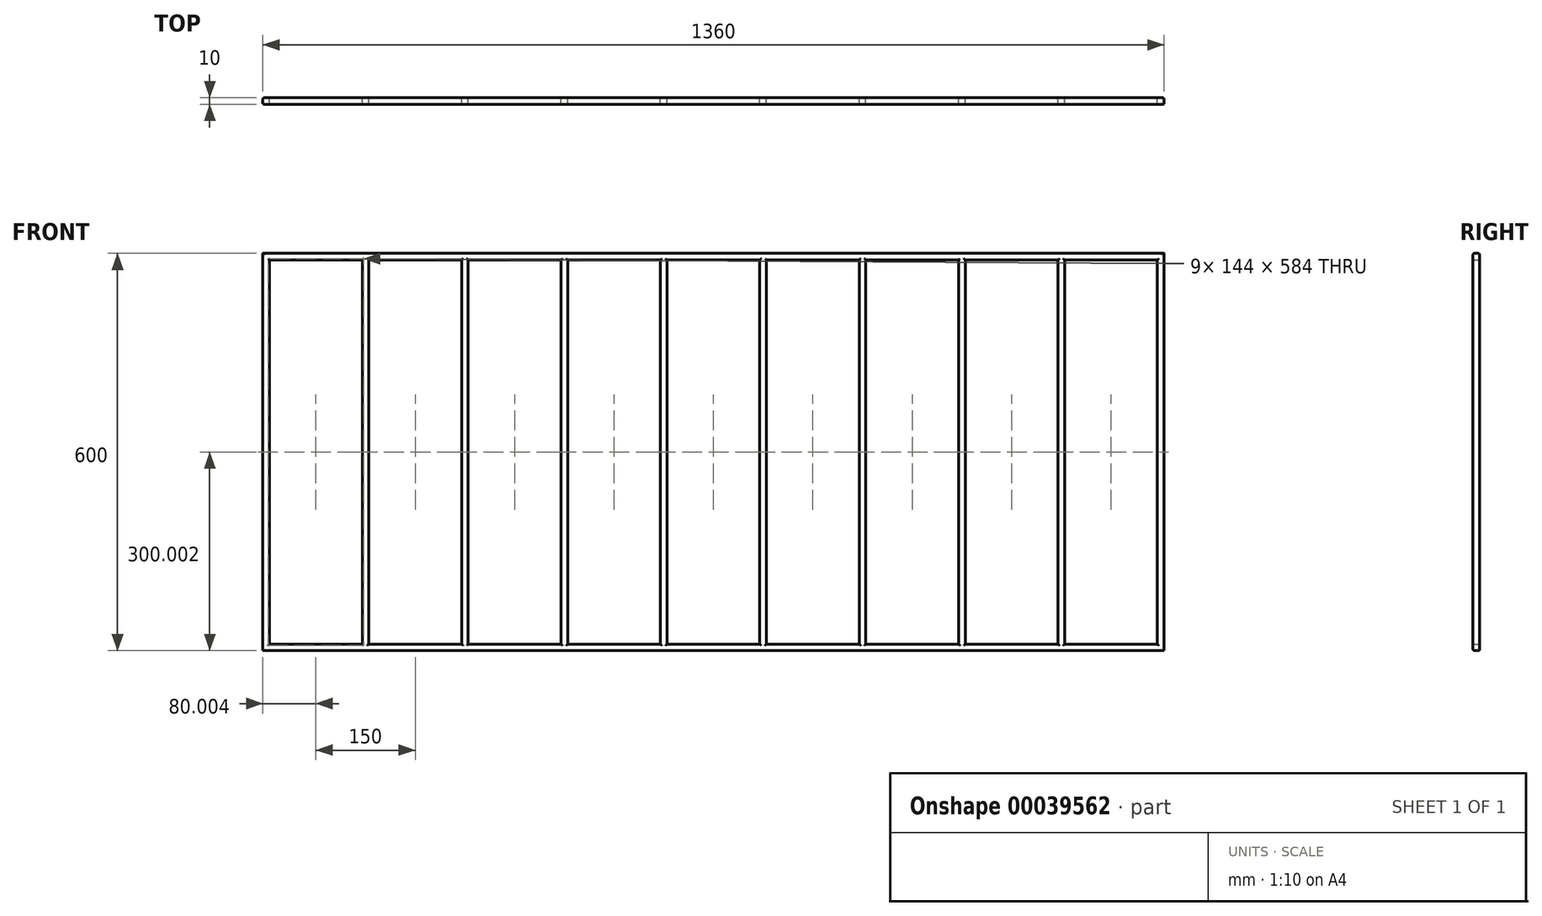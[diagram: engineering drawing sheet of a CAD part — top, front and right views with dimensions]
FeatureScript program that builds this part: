
annotation { "Feature Type Name" : "Feature", "Feature Type Description" : "" }
export const myFeature = defineFeature(function(context is Context, id is Id, definition is map)
    precondition{}
    {
        {
            var Q0;
            Q0=qCreatedBy(makeId("Front.planeOp"),FACE);
            var sketch = newSketch(context, id + "F0", { "sketchPlane" : qUnion([Q0])});
            skLineSegment(sketch, "E0.bottom", {"start": v(-58.93, -32.3) * mm, "end": v(1301.07, -32.3) * mm});
            skLineSegment(sketch, "E0.top", {"start": v(-58.93, 567.7) * mm, "end": v(1301.07, 567.7) * mm});
            skLineSegment(sketch, "E0.left", {"start": v(-58.93, -32.3) * mm, "end": v(-58.93, 567.7) * mm});
            skLineSegment(sketch, "E0.right", {"start": v(1301.07, -32.3) * mm, "end": v(1301.07, 567.7) * mm});
            skLineSegment(sketch, "E1.0", {"start": v(-48.93, 557.7) * mm, "end": v(91.07, 557.7) * mm});
            skLineSegment(sketch, "E2.0", {"start": v(-48.93, -22.3) * mm, "end": v(-48.93, 557.7) * mm});
            skLineSegment(sketch, "E3.0", {"start": v(1291.07, -22.3) * mm, "end": v(1291.07, 557.7) * mm});
            skLineSegment(sketch, "E4.0", {"start": v(-48.93, -22.3) * mm, "end": v(91.07, -22.3) * mm});
            skLineSegment(sketch, "E5.0", {"start": v(91.07, -22.3) * mm, "end": v(91.07, 557.7) * mm});
            skLineSegment(sketch, "E6.0", {"start": v(101.07, -22.3) * mm, "end": v(101.07, 557.7) * mm});
            skLineSegment(sketch, "E7.0", {"start": v(241.07, -22.3) * mm, "end": v(241.07, 557.7) * mm});
            skLineSegment(sketch, "E8.0", {"start": v(251.07, -22.3) * mm, "end": v(251.07, 557.7) * mm});
            skLineSegment(sketch, "E9.0", {"start": v(391.07, -22.3) * mm, "end": v(391.07, 557.7) * mm});
            skLineSegment(sketch, "E10.0", {"start": v(401.07, -22.3) * mm, "end": v(401.07, 557.7) * mm});
            skLineSegment(sketch, "E11.0", {"start": v(541.07, -22.3) * mm, "end": v(541.07, 557.7) * mm});
            skLineSegment(sketch, "E12.0", {"start": v(551.07, -22.3) * mm, "end": v(551.07, 557.7) * mm});
            skLineSegment(sketch, "E13.0", {"start": v(691.07, -22.3) * mm, "end": v(691.07, 557.7) * mm});
            skLineSegment(sketch, "E14.0", {"start": v(701.07, -22.3) * mm, "end": v(701.07, 557.7) * mm});
            skLineSegment(sketch, "E15.0", {"start": v(841.07, -22.3) * mm, "end": v(841.07, 557.7) * mm});
            skLineSegment(sketch, "E16.0", {"start": v(851.07, -22.3) * mm, "end": v(851.07, 557.7) * mm});
            skLineSegment(sketch, "E17.0", {"start": v(991.07, -22.3) * mm, "end": v(991.07, 557.7) * mm});
            skLineSegment(sketch, "E18.0", {"start": v(1001.07, -22.3) * mm, "end": v(1001.07, 557.7) * mm});
            skLineSegment(sketch, "E19.0", {"start": v(1141.07, -22.3) * mm, "end": v(1141.07, 557.7) * mm});
            skLineSegment(sketch, "E20.0", {"start": v(1151.07, -22.3) * mm, "end": v(1151.07, 557.7) * mm});
            skLineSegment(sketch, "E21.trimOffspring", {"start": v(101.07, 557.7) * mm, "end": v(241.07, 557.7) * mm});
            skLineSegment(sketch, "E22.trimOffspring", {"start": v(251.07, 557.7) * mm, "end": v(391.07, 557.7) * mm});
            skLineSegment(sketch, "E23.trimOffspring", {"start": v(401.07, 557.7) * mm, "end": v(541.07, 557.7) * mm});
            skLineSegment(sketch, "E24.trimOffspring", {"start": v(701.07, 557.7) * mm, "end": v(841.07, 557.7) * mm});
            skLineSegment(sketch, "E25.trimOffspring", {"start": v(551.07, 557.7) * mm, "end": v(691.07, 557.7) * mm});
            skLineSegment(sketch, "E26.trimOffspring", {"start": v(1001.07, 557.7) * mm, "end": v(1141.07, 557.7) * mm});
            skLineSegment(sketch, "E27.trimOffspring", {"start": v(851.07, 557.7) * mm, "end": v(991.07, 557.7) * mm});
            skLineSegment(sketch, "E28.trimOffspring", {"start": v(1151.07, 557.7) * mm, "end": v(1291.07, 557.7) * mm});
            skLineSegment(sketch, "E29.trimOffspring", {"start": v(1001.07, -22.3) * mm, "end": v(1141.07, -22.3) * mm});
            skLineSegment(sketch, "E30.trimOffspring", {"start": v(1151.07, -22.3) * mm, "end": v(1291.07, -22.3) * mm});
            skLineSegment(sketch, "E31.trimOffspring", {"start": v(851.07, -22.3) * mm, "end": v(991.07, -22.3) * mm});
            skLineSegment(sketch, "E32.trimOffspring", {"start": v(701.07, -22.3) * mm, "end": v(841.07, -22.3) * mm});
            skLineSegment(sketch, "E33.trimOffspring", {"start": v(401.07, -22.3) * mm, "end": v(541.07, -22.3) * mm});
            skLineSegment(sketch, "E34.trimOffspring", {"start": v(551.07, -22.3) * mm, "end": v(691.07, -22.3) * mm});
            skLineSegment(sketch, "E35.trimOffspring", {"start": v(251.07, -22.3) * mm, "end": v(391.07, -22.3) * mm});
            skLineSegment(sketch, "E36.trimOffspring", {"start": v(101.07, -22.3) * mm, "end": v(241.07, -22.3) * mm});
            skSolve(sketch);
        }
        {
            var Q0;
            Q0=makeQuery(id+"F0.imprint","IMPRINT",FACE,{"disambiguationData":[TD([[makeQuery(id+"F0.imprint","IMPRINT",EDGE,{"derivedFrom":sQuery(id+"F0.wireOp",EDGE,"E0.bottom")}),1.0]])]});
            extrude(context, id + "F1", {"entities" : qUnion([Q0]), "depth" : 10 * mm});
        }
        {
            var Q0;
            Q0=makeQuery(id+"F1.opExtrude","CAP_EDGE",EDGE,{"disambiguationData":[OSD([sQuery(id+"F0.wireOp",EDGE,"E30.trimOffspring")])],"isStart":false});
            var Q1;
            Q1=makeQuery(id+"F1.opExtrude","CAP_EDGE",EDGE,{"disambiguationData":[OSD([sQuery(id+"F0.wireOp",EDGE,"E20.0")])],"isStart":false});
            var Q2;
            Q2=makeQuery(id+"F1.opExtrude","CAP_EDGE",EDGE,{"disambiguationData":[OSD([sQuery(id+"F0.wireOp",EDGE,"E29.trimOffspring")])],"isStart":false});
            var Q3;
            Q3=makeQuery(id+"F1.opExtrude","CAP_EDGE",EDGE,{"disambiguationData":[OSD([sQuery(id+"F0.wireOp",EDGE,"E19.0")])],"isStart":false});
            var Q4;
            Q4=makeQuery(id+"F1.opExtrude","CAP_EDGE",EDGE,{"disambiguationData":[OSD([sQuery(id+"F0.wireOp",EDGE,"E30.trimOffspring")])],"isStart":true});
            var Q5;
            Q5=makeQuery(id+"F1.opExtrude","CAP_EDGE",EDGE,{"disambiguationData":[OSD([sQuery(id+"F0.wireOp",EDGE,"E20.0")])],"isStart":true});
            var Q6;
            Q6=makeQuery(id+"F1.opExtrude","CAP_EDGE",EDGE,{"disambiguationData":[OSD([sQuery(id+"F0.wireOp",EDGE,"E0.bottom")])],"isStart":false});
            var Q7;
            Q7=makeQuery(id+"F1.opExtrude","CAP_EDGE",EDGE,{"disambiguationData":[OSD([sQuery(id+"F0.wireOp",EDGE,"E0.right")])],"isStart":false});
            var Q8;
            Q8=makeQuery(id+"F1.opExtrude","CAP_EDGE",EDGE,{"disambiguationData":[OSD([sQuery(id+"F0.wireOp",EDGE,"E0.right")])],"isStart":true});
            var Q9;
            Q9=makeQuery(id+"F1.opExtrude","CAP_EDGE",EDGE,{"disambiguationData":[OSD([sQuery(id+"F0.wireOp",EDGE,"E3.0")])],"isStart":false});
            var Q10;
            Q10=makeQuery(id+"F1.opExtrude","CAP_EDGE",EDGE,{"disambiguationData":[OSD([sQuery(id+"F0.wireOp",EDGE,"E0.bottom")])],"isStart":true});
            var Q11;
            Q11=makeQuery(id+"F1.opExtrude","CAP_EDGE",EDGE,{"disambiguationData":[OSD([sQuery(id+"F0.wireOp",EDGE,"E3.0")])],"isStart":true});
            var Q12;
            Q12=makeQuery(id+"F1.opExtrude","CAP_EDGE",EDGE,{"disambiguationData":[OSD([sQuery(id+"F0.wireOp",EDGE,"E19.0")])],"isStart":true});
            var Q13;
            Q13=makeQuery(id+"F1.opExtrude","CAP_EDGE",EDGE,{"disambiguationData":[OSD([sQuery(id+"F0.wireOp",EDGE,"E29.trimOffspring")])],"isStart":true});
            var Q14;
            Q14=makeQuery(id+"F1.opExtrude","CAP_EDGE",EDGE,{"disambiguationData":[OSD([sQuery(id+"F0.wireOp",EDGE,"E18.0")])],"isStart":true});
            var Q15;
            Q15=makeQuery(id+"F1.opExtrude","CAP_EDGE",EDGE,{"disambiguationData":[OSD([sQuery(id+"F0.wireOp",EDGE,"E17.0")])],"isStart":true});
            var Q16;
            Q16=makeQuery(id+"F1.opExtrude","CAP_EDGE",EDGE,{"disambiguationData":[OSD([sQuery(id+"F0.wireOp",EDGE,"E17.0")])],"isStart":false});
            var Q17;
            Q17=makeQuery(id+"F1.opExtrude","CAP_EDGE",EDGE,{"disambiguationData":[OSD([sQuery(id+"F0.wireOp",EDGE,"E31.trimOffspring")])],"isStart":true});
            var Q18;
            Q18=makeQuery(id+"F1.opExtrude","CAP_EDGE",EDGE,{"disambiguationData":[OSD([sQuery(id+"F0.wireOp",EDGE,"E15.0")])],"isStart":true});
            var Q19;
            Q19=makeQuery(id+"F1.opExtrude","CAP_EDGE",EDGE,{"disambiguationData":[OSD([sQuery(id+"F0.wireOp",EDGE,"E15.0")])],"isStart":false});
            var Q20;
            Q20=makeQuery(id+"F1.opExtrude","CAP_EDGE",EDGE,{"disambiguationData":[OSD([sQuery(id+"F0.wireOp",EDGE,"E32.trimOffspring")])],"isStart":true});
            var Q21;
            Q21=makeQuery(id+"F1.opExtrude","CAP_EDGE",EDGE,{"disambiguationData":[OSD([sQuery(id+"F0.wireOp",EDGE,"E16.0")])],"isStart":true});
            var Q22;
            Q22=makeQuery(id+"F1.opExtrude","CAP_EDGE",EDGE,{"disambiguationData":[OSD([sQuery(id+"F0.wireOp",EDGE,"E14.0")])],"isStart":true});
            var Q23;
            Q23=makeQuery(id+"F1.opExtrude","CAP_EDGE",EDGE,{"disambiguationData":[OSD([sQuery(id+"F0.wireOp",EDGE,"E13.0")])],"isStart":true});
            var Q24;
            Q24=makeQuery(id+"F1.opExtrude","CAP_EDGE",EDGE,{"disambiguationData":[OSD([sQuery(id+"F0.wireOp",EDGE,"E13.0")])],"isStart":false});
            var Q25;
            Q25=makeQuery(id+"F1.opExtrude","CAP_EDGE",EDGE,{"disambiguationData":[OSD([sQuery(id+"F0.wireOp",EDGE,"E34.trimOffspring")])],"isStart":true});
            var Q26;
            Q26=makeQuery(id+"F1.opExtrude","CAP_EDGE",EDGE,{"disambiguationData":[OSD([sQuery(id+"F0.wireOp",EDGE,"E12.0")])],"isStart":true});
            var Q27;
            Q27=makeQuery(id+"F1.opExtrude","CAP_EDGE",EDGE,{"disambiguationData":[OSD([sQuery(id+"F0.wireOp",EDGE,"E11.0")])],"isStart":true});
            var Q28;
            Q28=makeQuery(id+"F1.opExtrude","CAP_EDGE",EDGE,{"disambiguationData":[OSD([sQuery(id+"F0.wireOp",EDGE,"E11.0")])],"isStart":false});
            var Q29;
            Q29=makeQuery(id+"F1.opExtrude","CAP_EDGE",EDGE,{"disambiguationData":[OSD([sQuery(id+"F0.wireOp",EDGE,"E33.trimOffspring")])],"isStart":true});
            var Q30;
            Q30=makeQuery(id+"F1.opExtrude","CAP_EDGE",EDGE,{"disambiguationData":[OSD([sQuery(id+"F0.wireOp",EDGE,"E10.0")])],"isStart":true});
            var Q31;
            Q31=makeQuery(id+"F1.opExtrude","CAP_EDGE",EDGE,{"disambiguationData":[OSD([sQuery(id+"F0.wireOp",EDGE,"E9.0")])],"isStart":true});
            var Q32;
            Q32=makeQuery(id+"F1.opExtrude","CAP_EDGE",EDGE,{"disambiguationData":[OSD([sQuery(id+"F0.wireOp",EDGE,"E35.trimOffspring")])],"isStart":true});
            var Q33;
            Q33=makeQuery(id+"F1.opExtrude","CAP_EDGE",EDGE,{"disambiguationData":[OSD([sQuery(id+"F0.wireOp",EDGE,"E9.0")])],"isStart":false});
            var Q34;
            Q34=makeQuery(id+"F1.opExtrude","CAP_EDGE",EDGE,{"disambiguationData":[OSD([sQuery(id+"F0.wireOp",EDGE,"E8.0")])],"isStart":true});
            var Q35;
            Q35=makeQuery(id+"F1.opExtrude","CAP_EDGE",EDGE,{"disambiguationData":[OSD([sQuery(id+"F0.wireOp",EDGE,"E7.0")])],"isStart":true});
            var Q36;
            Q36=makeQuery(id+"F1.opExtrude","CAP_EDGE",EDGE,{"disambiguationData":[OSD([sQuery(id+"F0.wireOp",EDGE,"E7.0")])],"isStart":false});
            var Q37;
            Q37=makeQuery(id+"F1.opExtrude","CAP_EDGE",EDGE,{"disambiguationData":[OSD([sQuery(id+"F0.wireOp",EDGE,"E36.trimOffspring")])],"isStart":true});
            var Q38;
            Q38=makeQuery(id+"F1.opExtrude","CAP_EDGE",EDGE,{"disambiguationData":[OSD([sQuery(id+"F0.wireOp",EDGE,"E6.0")])],"isStart":true});
            var Q39;
            Q39=makeQuery(id+"F1.opExtrude","CAP_EDGE",EDGE,{"disambiguationData":[OSD([sQuery(id+"F0.wireOp",EDGE,"E5.0")])],"isStart":true});
            var Q40;
            Q40=makeQuery(id+"F1.opExtrude","CAP_EDGE",EDGE,{"disambiguationData":[OSD([sQuery(id+"F0.wireOp",EDGE,"E5.0")])],"isStart":false});
            var Q41;
            Q41=makeQuery(id+"F1.opExtrude","CAP_EDGE",EDGE,{"disambiguationData":[OSD([sQuery(id+"F0.wireOp",EDGE,"E4.0")])],"isStart":true});
            var Q42;
            Q42=makeQuery(id+"F1.opExtrude","CAP_EDGE",EDGE,{"disambiguationData":[OSD([sQuery(id+"F0.wireOp",EDGE,"E2.0")])],"isStart":true});
            var Q43;
            Q43=makeQuery(id+"F1.opExtrude","CAP_EDGE",EDGE,{"disambiguationData":[OSD([sQuery(id+"F0.wireOp",EDGE,"E0.left")])],"isStart":true});
            var Q44;
            Q44=makeQuery(id+"F1.opExtrude","CAP_EDGE",EDGE,{"disambiguationData":[OSD([sQuery(id+"F0.wireOp",EDGE,"E0.left")])],"isStart":false});
            var Q45;
            Q45=makeQuery(id+"F1.opExtrude","CAP_EDGE",EDGE,{"disambiguationData":[OSD([sQuery(id+"F0.wireOp",EDGE,"E1.0")])],"isStart":false});
            var Q46;
            Q46=makeQuery(id+"F1.opExtrude","CAP_EDGE",EDGE,{"disambiguationData":[OSD([sQuery(id+"F0.wireOp",EDGE,"E0.top")])],"isStart":true});
            var Q47;
            Q47=makeQuery(id+"F1.opExtrude","CAP_EDGE",EDGE,{"disambiguationData":[OSD([sQuery(id+"F0.wireOp",EDGE,"E21.trimOffspring")])],"isStart":true});
            var Q48;
            Q48=makeQuery(id+"F1.opExtrude","CAP_EDGE",EDGE,{"disambiguationData":[OSD([sQuery(id+"F0.wireOp",EDGE,"E21.trimOffspring")])],"isStart":false});
            var Q49;
            Q49=makeQuery(id+"F1.opExtrude","CAP_EDGE",EDGE,{"disambiguationData":[OSD([sQuery(id+"F0.wireOp",EDGE,"E23.trimOffspring")])],"isStart":false});
            var Q50;
            Q50=makeQuery(id+"F1.opExtrude","CAP_EDGE",EDGE,{"disambiguationData":[OSD([sQuery(id+"F0.wireOp",EDGE,"E23.trimOffspring")])],"isStart":true});
            var Q51;
            Q51=makeQuery(id+"F1.opExtrude","CAP_EDGE",EDGE,{"disambiguationData":[OSD([sQuery(id+"F0.wireOp",EDGE,"E22.trimOffspring")])],"isStart":false});
            var Q52;
            Q52=makeQuery(id+"F1.opExtrude","CAP_EDGE",EDGE,{"disambiguationData":[OSD([sQuery(id+"F0.wireOp",EDGE,"E22.trimOffspring")])],"isStart":true});
            var Q53;
            Q53=makeQuery(id+"F1.opExtrude","CAP_EDGE",EDGE,{"disambiguationData":[OSD([sQuery(id+"F0.wireOp",EDGE,"E24.trimOffspring")])],"isStart":false});
            var Q54;
            Q54=makeQuery(id+"F1.opExtrude","CAP_EDGE",EDGE,{"disambiguationData":[OSD([sQuery(id+"F0.wireOp",EDGE,"E24.trimOffspring")])],"isStart":true});
            var Q55;
            Q55=makeQuery(id+"F1.opExtrude","CAP_EDGE",EDGE,{"disambiguationData":[OSD([sQuery(id+"F0.wireOp",EDGE,"E25.trimOffspring")])],"isStart":false});
            var Q56;
            Q56=makeQuery(id+"F1.opExtrude","CAP_EDGE",EDGE,{"disambiguationData":[OSD([sQuery(id+"F0.wireOp",EDGE,"E25.trimOffspring")])],"isStart":true});
            var Q57;
            Q57=makeQuery(id+"F1.opExtrude","CAP_EDGE",EDGE,{"disambiguationData":[OSD([sQuery(id+"F0.wireOp",EDGE,"E26.trimOffspring")])],"isStart":false});
            var Q58;
            Q58=makeQuery(id+"F1.opExtrude","CAP_EDGE",EDGE,{"disambiguationData":[OSD([sQuery(id+"F0.wireOp",EDGE,"E26.trimOffspring")])],"isStart":true});
            var Q59;
            Q59=makeQuery(id+"F1.opExtrude","CAP_EDGE",EDGE,{"disambiguationData":[OSD([sQuery(id+"F0.wireOp",EDGE,"E27.trimOffspring")])],"isStart":false});
            var Q60;
            Q60=makeQuery(id+"F1.opExtrude","CAP_EDGE",EDGE,{"disambiguationData":[OSD([sQuery(id+"F0.wireOp",EDGE,"E27.trimOffspring")])],"isStart":true});
            var Q61;
            Q61=makeQuery(id+"F1.opExtrude","CAP_EDGE",EDGE,{"disambiguationData":[OSD([sQuery(id+"F0.wireOp",EDGE,"E28.trimOffspring")])],"isStart":false});
            var Q62;
            Q62=makeQuery(id+"F1.opExtrude","CAP_EDGE",EDGE,{"disambiguationData":[OSD([sQuery(id+"F0.wireOp",EDGE,"E28.trimOffspring")])],"isStart":true});
            var Q63;
            Q63=makeQuery(id+"F1.opExtrude","CAP_EDGE",EDGE,{"disambiguationData":[OSD([sQuery(id+"F0.wireOp",EDGE,"E18.0")])],"isStart":false});
            var Q64;
            Q64=makeQuery(id+"F1.opExtrude","CAP_EDGE",EDGE,{"disambiguationData":[OSD([sQuery(id+"F0.wireOp",EDGE,"E16.0")])],"isStart":false});
            var Q65;
            Q65=makeQuery(id+"F1.opExtrude","CAP_EDGE",EDGE,{"disambiguationData":[OSD([sQuery(id+"F0.wireOp",EDGE,"E14.0")])],"isStart":false});
            var Q66;
            Q66=makeQuery(id+"F1.opExtrude","CAP_EDGE",EDGE,{"disambiguationData":[OSD([sQuery(id+"F0.wireOp",EDGE,"E12.0")])],"isStart":false});
            var Q67;
            Q67=makeQuery(id+"F1.opExtrude","CAP_EDGE",EDGE,{"disambiguationData":[OSD([sQuery(id+"F0.wireOp",EDGE,"E10.0")])],"isStart":false});
            var Q68;
            Q68=makeQuery(id+"F1.opExtrude","CAP_EDGE",EDGE,{"disambiguationData":[OSD([sQuery(id+"F0.wireOp",EDGE,"E8.0")])],"isStart":false});
            var Q69;
            Q69=makeQuery(id+"F1.opExtrude","CAP_EDGE",EDGE,{"disambiguationData":[OSD([sQuery(id+"F0.wireOp",EDGE,"E6.0")])],"isStart":false});
            var Q70;
            Q70=makeQuery(id+"F1.opExtrude","CAP_EDGE",EDGE,{"disambiguationData":[OSD([sQuery(id+"F0.wireOp",EDGE,"E2.0")])],"isStart":false});
            var Q71;
            Q71=makeQuery(id+"F1.opExtrude","CAP_EDGE",EDGE,{"disambiguationData":[OSD([sQuery(id+"F0.wireOp",EDGE,"E0.top")])],"isStart":false});
            var Q72;
            Q72=makeQuery(id+"F1.opExtrude","CAP_EDGE",EDGE,{"disambiguationData":[OSD([sQuery(id+"F0.wireOp",EDGE,"E31.trimOffspring")])],"isStart":false});
            var Q73;
            Q73=makeQuery(id+"F1.opExtrude","CAP_EDGE",EDGE,{"disambiguationData":[OSD([sQuery(id+"F0.wireOp",EDGE,"E32.trimOffspring")])],"isStart":false});
            var Q74;
            Q74=makeQuery(id+"F1.opExtrude","CAP_EDGE",EDGE,{"disambiguationData":[OSD([sQuery(id+"F0.wireOp",EDGE,"E34.trimOffspring")])],"isStart":false});
            var Q75;
            Q75=makeQuery(id+"F1.opExtrude","CAP_EDGE",EDGE,{"disambiguationData":[OSD([sQuery(id+"F0.wireOp",EDGE,"E33.trimOffspring")])],"isStart":false});
            var Q76;
            Q76=makeQuery(id+"F1.opExtrude","CAP_EDGE",EDGE,{"disambiguationData":[OSD([sQuery(id+"F0.wireOp",EDGE,"E35.trimOffspring")])],"isStart":false});
            var Q77;
            Q77=makeQuery(id+"F1.opExtrude","CAP_EDGE",EDGE,{"disambiguationData":[OSD([sQuery(id+"F0.wireOp",EDGE,"E36.trimOffspring")])],"isStart":false});
            var Q78;
            Q78=makeQuery(id+"F1.opExtrude","CAP_EDGE",EDGE,{"disambiguationData":[OSD([sQuery(id+"F0.wireOp",EDGE,"E4.0")])],"isStart":false});
            var Q79;
            Q79=makeQuery(id+"F1.opExtrude","CAP_EDGE",EDGE,{"disambiguationData":[OSD([sQuery(id+"F0.wireOp",EDGE,"E1.0")])],"isStart":true});
            fillet(context, id + "F2", {"entities" : qUnion([Q0, Q1, Q2, Q3, Q4, Q5, Q6, Q7, Q8, Q9, Q10, Q11, Q12, Q13, Q14, Q15, Q16, Q17, Q18, Q19, Q20, Q21, Q22, Q23, Q24, Q25, Q26, Q27, Q28, Q29, Q30, Q31, Q32, Q33, Q34, Q35, Q36, Q37, Q38, Q39, Q40, Q41, Q42, Q43, Q44, Q45, Q46, Q47, Q48, Q49, Q50, Q51, Q52, Q53, Q54, Q55, Q56, Q57, Q58, Q59, Q60, Q61, Q62, Q63, Q64, Q65, Q66, Q67, Q68, Q69, Q70, Q71, Q72, Q73, Q74, Q75, Q76, Q77, Q78, Q79]), "radius" : 2 * mm, "tangentPropagation" : true, "allowEdgeOverflow" : false});
        }
    });
